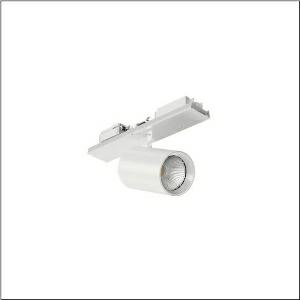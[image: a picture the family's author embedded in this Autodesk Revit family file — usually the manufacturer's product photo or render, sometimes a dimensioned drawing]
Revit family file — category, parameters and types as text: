
# Revit family: licross_r__spot_31_51sl12da45b_e1b3
name_source: partatom
category: Lighting Fixtures
units: mm (PartAtom-declared; Revit-internal decimal feet)

## family parameters
Cut with Voids When Loaded = No
Host = Face
Light Source = No
Part Type = Normal
Room Calculation Point = No
Round Connector Dimension = Use Diameter
Shared = No

## types (1)
- --- (1 x LED, 5140 lm, 43.9 W, 4000K)
    Apparent Load = 44 VA
    CIE Flux Codes = 93 97 99 100 100
    Color Rendering = 90
    Color Temperature = 4000K
    Default Elevation = 1800 mm
    Description = Licross® Spot 31, directional spotlight, light control with lens, of plastic, LED rated luminous flux: 5.140lm, light colour: 940, with plug, 5-pole, mains connection: 220..240V, AC, 50/60Hz, of aluminium, traffic white (RAL 9016), length: 300mm, diameter: 90mm, protection rating (complete): IP20, insulation class (complete): insulation class I (protective earthing), certification: CE, packaging unit: 1 piece
    Height = 175 mm
    Lamp = 1 x LED
    Lamp Light Flux = 5140 lm
    Lamp Power = 43.9 W
    Lamp count = 1
    Length = 90 mm
    Luminous efficacy = 117 lm/W
    Manufacturer = Siteco
    ModVariant = No
    Model = 51SL12DA45B
    Mounting Place = Ceiling
    Mounting Type = Pendant
    Number of Poles = 1
    OnlyDefault = Yes
    Power Factor = 1
    Product Name = Licross® Spot 31
    Product group = directional spotlight
    ProductGroupID = 906
    Protection Class = Protection class I
    Protection Degree = IP 20
    RLX_Detail_Level = 1
    RLX_Emergency_Light_Flux = 0 lm
    RLX_Emergency_Type = 0
    RLX_Emergency_Type_DB = No
    RlxData = <blob elided: 14817 chars, md5=89a4916b>
    Socket = socket
    Standby Power = 0 W
    System Light Flux = 5140 lm
    System Power = 44 W
    Type Comments = factory setting: luminous flux: 100 % | (ON | ON | ON) | 1050 mA
    Type Image = l_1245720.jpg
    URL = http://relux.com
    VarID = @adj_132520
    Voltage = 0 V
    Weight = 0.00 kg
    Width = 0 mm  [stored 0 ft]

note: [stored X ft] marks values corroborated as IEEE doubles in the binary element streams (Revit-internal decimal feet)

## geometry (parser evidence)
native form markers: Sweep x10
no freeform markers — native parametric forms only
